# Revit family: Gira_565103
name_source: partatom
category: Allgemeines Modell
revit_build: Autodesk Revit 2017 (Build: 20160225_1515(x64)
units: mm (PartAtom-declared; Revit-internal decimal feet)

## family parameters
Basisbauteil = Fläche
Beim Laden mit Abzugskörper schneiden = Nein
Bemaßung runder Anschluss = Durchmesser verwenden
Gemeinsam genutzt = Nein
Kann Basisbauteil für Bewehrung sein = Nein
Raumberechnungspunkt = Nein
Teiletyp = Normal

## types (1)
- Gira_565103
    Ausführung der Oberfläche = glänzend
    BIM = https://media.stage.bim.site 2fach_Kpl. Eins. RW.rfa
    Befestigungsart = Befestigung mit Schraube
    Beschreibung = Einsatz SAT-F-Buchse 2fach Kupplung Reinweiß glänzend Hinweise : - Nur für Schraubbefestigung. - Achtung! Bauraum für Stecker und Biegeradien beachten. - Bei Einsätzen mit Kupplungen beachten:   Nicht für Kanalinstallation und Standard-Gerätedose geeignet.   Anschluss mit Winkelsteckern empfohlen. - Installationsempfehlung:   Kaiser Elektronic-Dosen   Unterputz-Montage: Kaiser Best.-Nr.: 1068-02   Hohlwandmontage: Kaiser Best.-Nr.: 9062-94   Betoninstallation: Kaiser Best.-Nr.: 1268-40
    Beschriftungsfeld = ohne Beschriftungsfeld
    Datenblatt = https://katalog.gira.de
    Farbe = weiß
    GTIN = 4010337461005
    Geeignet für Schutzart (IP) = IP20
    HAN = 565103
    Halogenfrei = Nein
    Hersteller = Gira
    Lüsterklemme = Nein
    Mit Aufdruck = Nein
    Mit Klappdeckel = Nein
    Mit Staubschutz = Nein
    Mit Zugentlastung = Nein
    Montageart = Unterputz
    Oberfläche = sonstige
    Produktseite = http://katalog.gira.de
    RAL-Nummer (ähnlich) = 9010
    Tragring = Ja
    Transparent = Nein
    Typname = SAT-F-Buchse 2f Kpl. Einsatz Reinweiß
    URL = https://www.gira.de
    Verwendung = Sat
    Vorgabe-Ansicht = 1219 mm
    Werkstoff = sonstige
    Werkstoffgüte = sonstige
    Zusammenstellung = Zentralplatte

## geometry (parser evidence)
native form markers: Sweep x2
no freeform markers — native parametric forms only
